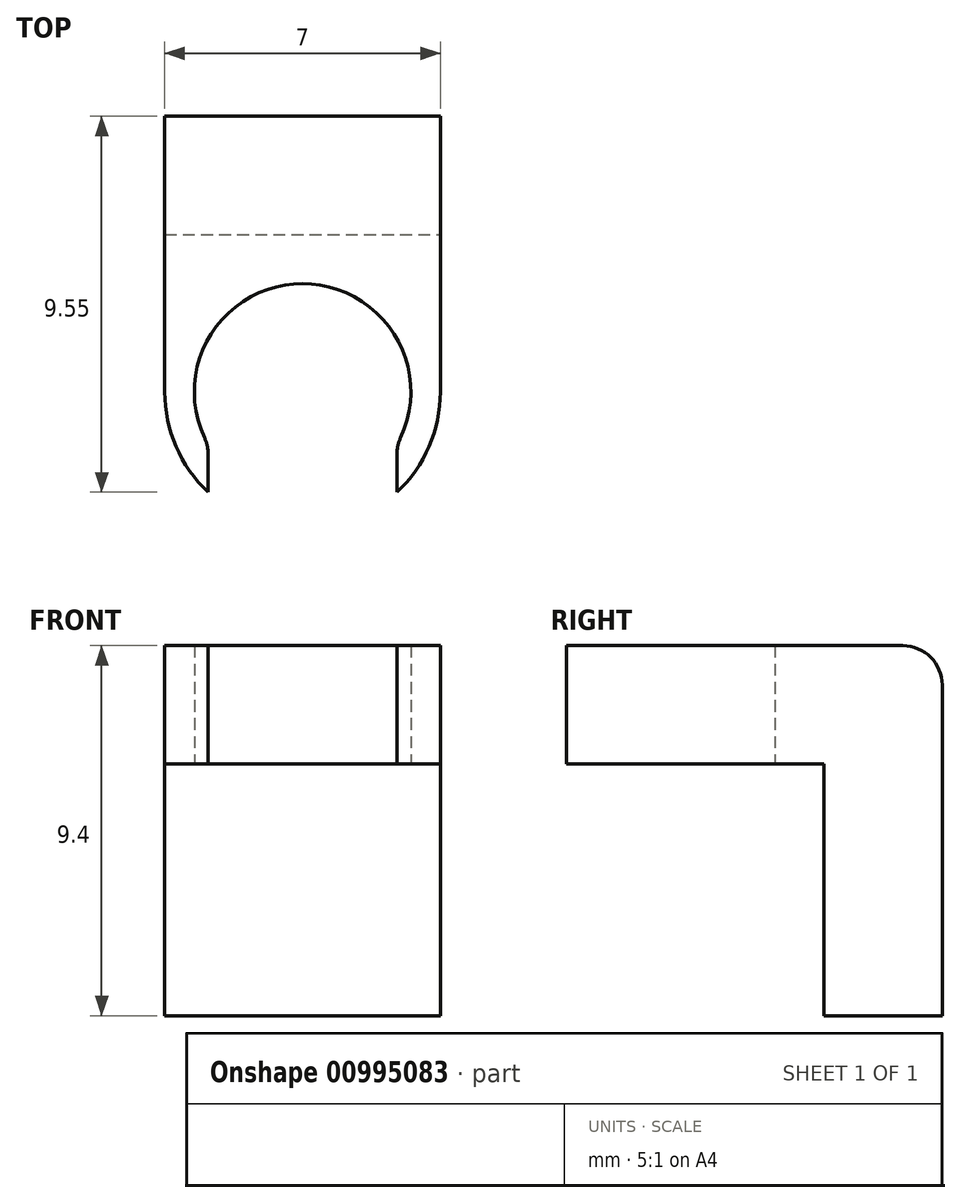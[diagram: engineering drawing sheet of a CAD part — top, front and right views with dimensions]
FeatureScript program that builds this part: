
annotation { "Feature Type Name" : "Feature", "Feature Type Description" : "" }
export const myFeature = defineFeature(function(context is Context, id is Id, definition is map)
    precondition{}
    {
        {
            var Q0;
            Q0=qCreatedBy(makeId("Top.planeOp"),FACE);
            var sketch = newSketch(context, id + "F0", { "sketchPlane" : qUnion([Q0])});
            skCircle(sketch, "E0", {"center": v(0, 0) * mm, "radius": 2.75 * mm});
            skLineSegment(sketch, "E1.bottom", {"start": v(-2.4, 0) * mm, "end": v(2.4, 0) * mm});
            skLineSegment(sketch, "E1.top", {"start": v(-2.4, -3.5) * mm, "end": v(2.4, -3.5) * mm});
            skLineSegment(sketch, "E1.left", {"start": v(-2.4, 0) * mm, "end": v(-2.4, -3.5) * mm});
            skLineSegment(sketch, "E1.right", {"start": v(2.4, 0) * mm, "end": v(2.4, -3.5) * mm});
            skCircle(sketch, "E2", {"center": v(0, 0) * mm, "radius": 3.5 * mm});
            skLineSegment(sketch, "E3.bottom", {"start": v(-3.5, 0) * mm, "end": v(3.5, 0) * mm});
            skLineSegment(sketch, "E3.top", {"start": v(-3.5, 4) * mm, "end": v(3.5, 4) * mm});
            skLineSegment(sketch, "E3.left", {"start": v(-3.5, 0) * mm, "end": v(-3.5, 4) * mm});
            skLineSegment(sketch, "E3.right", {"start": v(3.5, 0) * mm, "end": v(3.5, 4) * mm});
            skSolve(sketch);
        }
        {
            var Q0;
            {var subQ0=sQuery(id+"F0.wireOp",EDGE,"E1.left");var subQ1=sQuery(id+"F0.wireOp",EDGE,"E0");var subQ2=makeQuery(id+"F0.imprint","INTERSECT",VERTEX,{"derivedFrom":[subQ1,subQ0]});Q0=makeQuery(id+"F0.imprint","IMPRINT",FACE,{"disambiguationData":[TD([[makeQuery(id+"F0.imprint","IMPRINT",EDGE,{"disambiguationData":[TD([[subQ2,1.0]])],"derivedFrom":subQ1}),-1.0]])]});}
            var Q1;
            {var subQ0=sQuery(id+"F0.wireOp",EDGE,"E3.bottom");var subQ1=sQuery(id+"F0.wireOp",EDGE,"E0");var subQ2=makeQuery(id+"F0.imprint","INTERSECT",VERTEX,{"disambiguationData":[OD(1.0)],"derivedFrom":[subQ1,subQ0]});Q1=makeQuery(id+"F0.imprint","IMPRINT",FACE,{"disambiguationData":[TD([[makeQuery(id+"F0.imprint","IMPRINT",EDGE,{"disambiguationData":[TD([[subQ2,1.0]])],"derivedFrom":subQ1}),-1.0]])]});}
            var Q2;
            {var subQ0=sQuery(id+"F0.wireOp",EDGE,"E3.bottom");var subQ1=sQuery(id+"F0.wireOp",EDGE,"E0");var subQ2=makeQuery(id+"F0.imprint","INTERSECT",VERTEX,{"disambiguationData":[OD(0.0)],"derivedFrom":[subQ1,subQ0]});Q2=makeQuery(id+"F0.imprint","IMPRINT",FACE,{"disambiguationData":[TD([[makeQuery(id+"F0.imprint","IMPRINT",EDGE,{"disambiguationData":[TD([[subQ2,1.0]])],"derivedFrom":subQ1}),-1.0]])]});}
            var Q3;
            Q3=makeQuery(id+"F0.imprint","IMPRINT",FACE,{"disambiguationData":[TD([[makeQuery(id+"F0.imprint","IMPRINT",EDGE,{"derivedFrom":sQuery(id+"F0.wireOp",EDGE,"E3.top")}),-1.0]])]});
            extrude(context, id + "F1", {"entities" : qUnion([Q0, Q1, Q2, Q3]), "depth" : 3 * mm, "offsetDistance" : 25 * mm});
        }
        {
            var Q0;
            Q0=makeQuery(id+"F1.opExtrude","SWEPT_FACE",FACE,{"disambiguationData":[OSD([sQuery(id+"F0.wireOp",EDGE,"E3.top")])]});
            var sketch = newSketch(context, id + "F2", { "sketchPlane" : qUnion([Q0])});
            skLineSegment(sketch, "E4.bottom", {"start": v(3.5, 3) * mm, "end": v(-3.5, 3) * mm});
            skLineSegment(sketch, "E4.top", {"start": v(3.5, -6.4) * mm, "end": v(-3.5, -6.4) * mm});
            skLineSegment(sketch, "E4.left", {"start": v(3.5, 3) * mm, "end": v(3.5, -6.4) * mm});
            skLineSegment(sketch, "E4.right", {"start": v(-3.5, 3) * mm, "end": v(-3.5, -6.4) * mm});
            skSolve(sketch);
        }
        {
            var Q0;
            Q0 = qSketchRegion(id + "F2", true);
            extrude(context, id + "F3", {"entities" : qUnion([Q0]), "operationType" : NewBodyOperationType.ADD, "depth" : 3 * mm, "offsetDistance" : 25 * mm});
        }
        {
            var Q0;
            Q0=makeQuery(id+"F3.opExtrude","CAP_EDGE",EDGE,{"disambiguationData":[OSD([sQuery(id+"F2.wireOp",EDGE,"E4.bottom")])],"isStart":false});
            var Q1;
            Q1=makeQuery(id+"F1.opExtrude","SWEPT_EDGE",EDGE,{"disambiguationData":[OSD([sQuery(id+"F0.wireOp",EDGE,"E0"),sQuery(id+"F0.wireOp",EDGE,"E1.left")])]});
            var Q2;
            Q2=makeQuery(id+"F1.opExtrude","SWEPT_EDGE",EDGE,{"disambiguationData":[OSD([sQuery(id+"F0.wireOp",EDGE,"E0"),sQuery(id+"F0.wireOp",EDGE,"E1.right")])]});
            fillet(context, id + "F4", {"entities" : qUnion([Q0, Q1, Q2]), "radius" : 1 * mm, "tangentPropagation" : true, "allowEdgeOverflow" : false});
        }
    });
